# Revit family: Safety & Protection_Barrier_UltiGroup_Safe-T Vertical
name_source: partatom
category: Specialty Equipment
revit_build: Autodesk Revit Architecture 2016 (Build: 20150220_1215(x64)
units: mm (PartAtom-declared; Revit-internal decimal feet)

## family parameters
Cut with Voids When Loaded = No
Host = Face
OmniClass Number = 23.50.70.00
OmniClass Title = Loading Dock Equipment
Part Type = Normal
Room Calculation Point = No
Round Connector Dimension = Use Diameter
Shared = No

## types (2) — shared parameters
Description = Loading Dock Vertical Swinging Safety Barrier - Safe-T Gate Vertical
Fax = 07 846 2467
Manufacturer = UltiGroup
Maximum Clear Opening Width = 4975 mm
Model = Safe-T Gate Vertical
Send Message = http://ultigroup.co.nz
URL = www.ultigroup.co.nz
zero-valued in all types: Default Elevation, InstallationGroup_ANZRS, ModifiedIssue_ANZRS

## type names (no varying parameters)
- Type 1
- Type 2

## geometry (parser evidence)
native form markers: Blend x2, Sweep x2
no freeform markers — native parametric forms only
